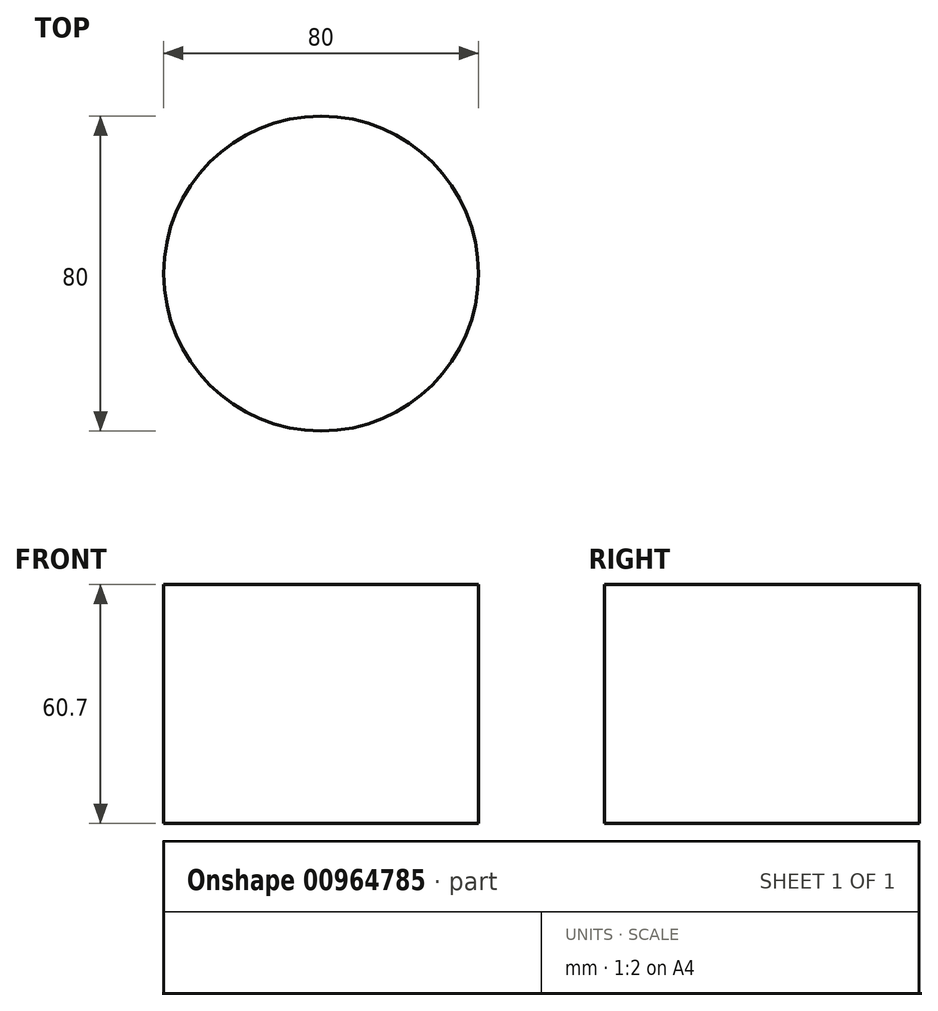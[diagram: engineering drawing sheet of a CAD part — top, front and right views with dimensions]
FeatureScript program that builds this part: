
annotation { "Feature Type Name" : "Feature", "Feature Type Description" : "" }
export const myFeature = defineFeature(function(context is Context, id is Id, definition is map)
    precondition{}
    {
        {
            var Q0;
            Q0=qCreatedBy(makeId("Top.planeOp"),FACE);
            var sketch = newSketch(context, id + "F0", { "sketchPlane" : qUnion([Q0])});
            skCircle(sketch, "E0", {"center": v(0, 0) * mm, "radius": 40 * mm});
            skSolve(sketch);
        }
        {
            var Q0;
            Q0=makeQuery(id+"F0.imprint","IMPRINT",FACE,{"disambiguationData":[TD([[makeQuery(id+"F0.imprint","IMPRINT",EDGE,{"derivedFrom":sQuery(id+"F0.wireOp",EDGE,"E0")}),1.0]])]});
            extrude(context, id + "F1", {"entities" : qUnion([Q0]), "depth" : 60.7 * mm, "offsetDistance" : 25 * mm});
        }
    });
